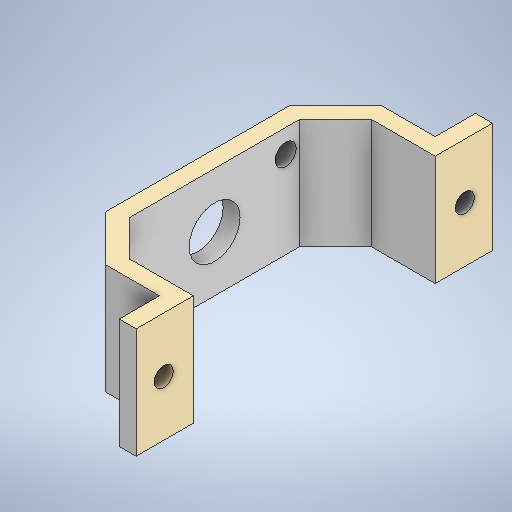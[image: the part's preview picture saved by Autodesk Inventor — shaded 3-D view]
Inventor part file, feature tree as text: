
AUTODESK INVENTOR PART (.ipt)
format: ipt  version: 2025 (Build 290162000, 162)  size: 300,544 bytes
history: native  units: in
note: dims shown in document units (in); Inventor stores cm internally (conversion verified against a paired STEP export)
features: sketch x7, extrude x5, other x1
ambient origin geometry x8: Origin, YZ Plane, XZ Plane, XY Plane, X Axis, Y Axis, Z Axis, Center Point
bodies: Solid1 (feature_tree)
feature tree (13):
  extrude  "Extrusion1"  Depth=0.5315in
  extrude  "Extrusion2"  Depth=1.0236in
  extrude  "Extrusion7"  Depth=0.5118in
  extrude  "Extrusion8"  Depth=0.3937in
  extrude  "Extrusion9"  Depth=0.5906in
  sketch  "Sketch1"  dims[d5=0.5315in d6=0.5315in]
  sketch  "Sketch2"  dims[d17=3.3071in d20=1.0236in d21=0.0in d23=0.1772in]
  sketch  "Sketch Rectangular Pattern2"  dims[d29=0.2559in d30=0.5118in]
  sketch  "Sketch7"  dims[d98=0.0in d100=0.5906in]
  sketch  "Sketch8"  dims[d101=0.5906in]
  sketch  "Sketch Circular Pattern2"  dims[d33=2.7953in d39=0.3937in d40=0.0in d91=0.7874in d93=2.7953in d94=0.3937in d96=0.3937in]
  sketch  "Sketch9"  dims[d103=135.0deg d104=135.0deg d106=0.9252in d107=0.1575in d108=0.4724in d109=1.6535in d110=0.5118in d111=3.3071in d112=0.3937in d113=0.0in d114=1.4449in d115=0.1969in d116=0.2165in d117=0.7874in d119=360.0deg d121=0.3937in d122=0.0in d123=0.315in d124=0.315in d125=0.1575in d126=0.0in d81=0.0in d82=0.0in d83=0.0in d84=0.0in]
  other  "Finish1"
